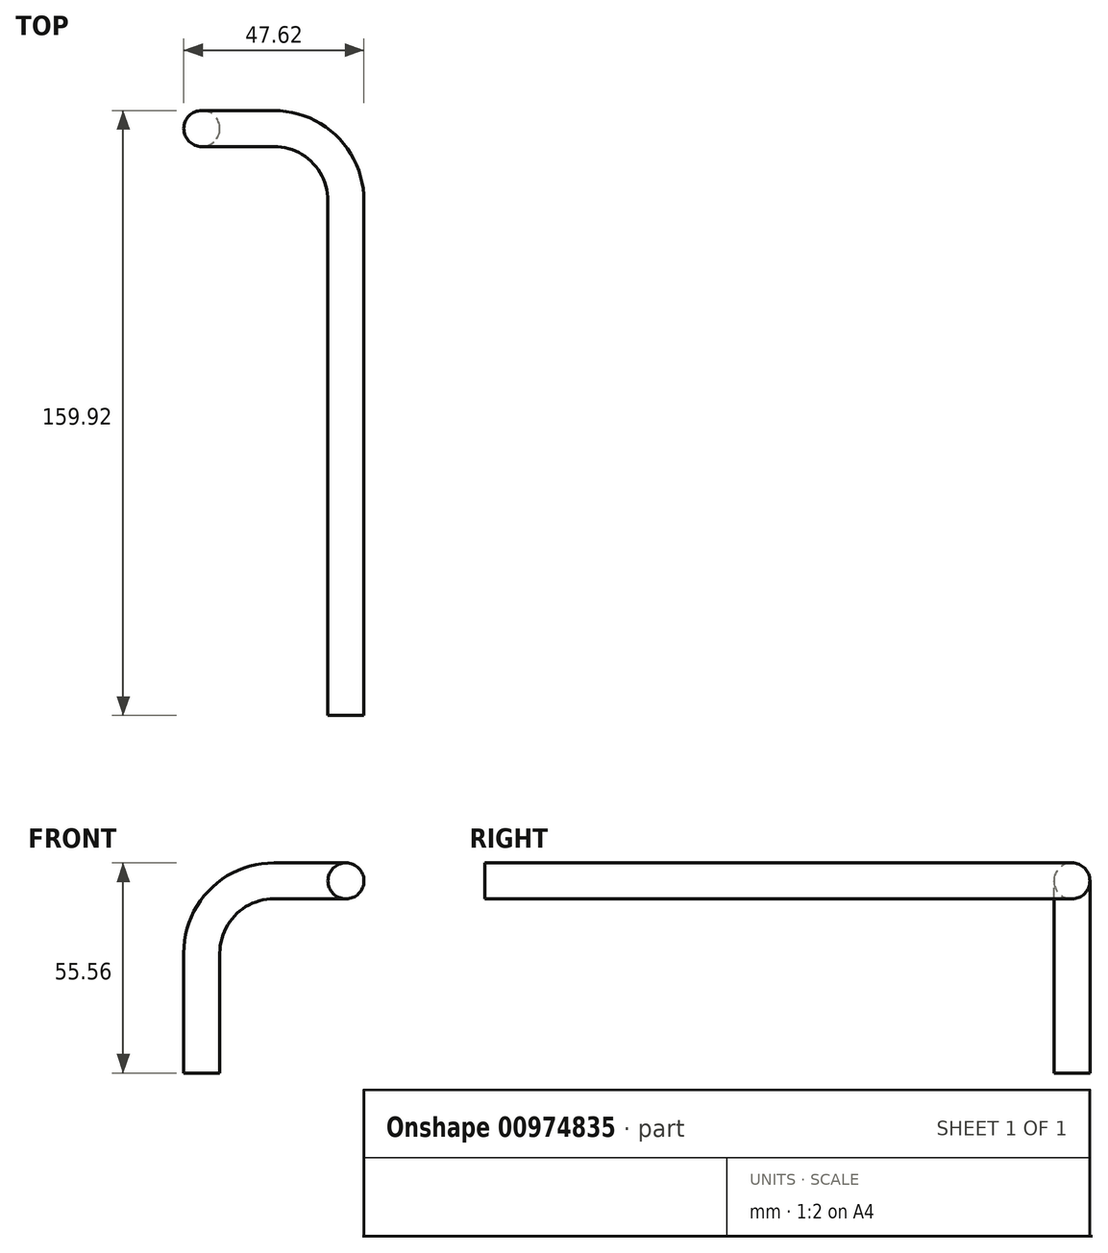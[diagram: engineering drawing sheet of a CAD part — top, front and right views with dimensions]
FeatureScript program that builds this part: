
annotation { "Feature Type Name" : "Feature", "Feature Type Description" : "" }
export const myFeature = defineFeature(function(context is Context, id is Id, definition is map)
    precondition{}
    {
        {
            var Q0;
            Q0=qCreatedBy(makeId("Front.planeOp"),FACE);
            var sketch = newSketch(context, id + "F0", { "sketchPlane" : qUnion([Q0])});
            skLineSegment(sketch, "E0", {"start": v(-19.05, -50.8) * mm, "end": v(-19.05, -19.05) * mm});
            skPoint(sketch, "E1.visualSharp", {"position": v(-19.05, 0) * mm});
            skArc(sketch, "E1.filletArc", {"start": v(0, 0) * mm, "mid": v(-13.47, -5.58) * mm, "end": v(-19.05, -19.05) * mm});
            skLineSegment(sketch, "E2", {"start": v(0, 0) * mm, "end": v(-19.05, 0) * mm, "construction": true});
            skSolve(sketch);
        }
        {
            var Q0;
            Q0=qCreatedBy(makeId("Top.planeOp"),FACE);
            var Q1;
            Q1=sQuery(id+"F0.wireOp",VERTEX,"E0.start");
            cPlane(context, id + "F1", {"entities" : qUnion([Q0, Q1]), "cplaneType" : CPlaneType.PLANE_POINT, "offset" : 25.4 * mm, "width" : 152.4 * mm, "height" : 152.4 * mm});
        }
        {
            var Q0;
            Q0=qCreatedBy(id+"F1.planeOp",FACE);
            var sketch = newSketch(context, id + "F2", { "sketchPlane" : qUnion([Q0])});
            skCircle(sketch, "E3", {"center": v(-19.05, 0) * mm, "radius": 4.76 * mm});
            skSolve(sketch);
        }
        {
            var Q0;
            Q0 = qSketchRegion(id + "F2", true);
            var Q1;
            Q1=sQuery(id+"F0.wireOp",EDGE,"E0");
            var Q2;
            Q2=sQuery(id+"F0.wireOp",EDGE,"E1.filletArc");
            sweep(context, id + "F3", {"profiles" : qUnion([Q0]), "path" : qUnion([Q1, Q2])});
        }
        {
            var Q0;
            Q0=qCreatedBy(makeId("Top.planeOp"),FACE);
            var sketch = newSketch(context, id + "F4", { "sketchPlane" : qUnion([Q0])});
            skLineSegment(sketch, "E4", {"start": v(19.05, -19.05) * mm, "end": v(19.05, -155.16) * mm});
            skPoint(sketch, "E5.visualSharp", {"position": v(19.05, -53.56) * mm});
            skArc(sketch, "E5.filletArc", {"start": v(19.05, -19.05) * mm, "mid": v(13.47, -5.58) * mm, "end": v(0, 0) * mm});
            skSolve(sketch);
        }
        {
            var Q0;
            Q0=makeQuery(id+"F3.opSweep","CAP_FACE",FACE,{"disambiguationData":[OSD([sQuery(id+"F0.wireOp",VERTEX,"E1.filletArc.start"),sQuery(id+"F2.wireOp",EDGE,"E3")])],"isStart":false});
            var sketch = newSketch(context, id + "F5", { "sketchPlane" : qUnion([Q0])});
            skCircle(sketch, "E6.0", {"center": v(0, 0) * mm, "radius": 4.76 * mm});
            skSolve(sketch);
        }
        {
            var Q0;
            Q0 = qSketchRegion(id + "F5", true);
            var Q1;
            Q1=sQuery(id+"F4.wireOp",EDGE,"E5.filletArc");
            var Q2;
            Q2=sQuery(id+"F4.wireOp",EDGE,"E4");
            sweep(context, id + "F6", {"operationType" : NewBodyOperationType.ADD, "profiles" : qUnion([Q0]), "path" : qUnion([Q1, Q2])});
        }
    });
